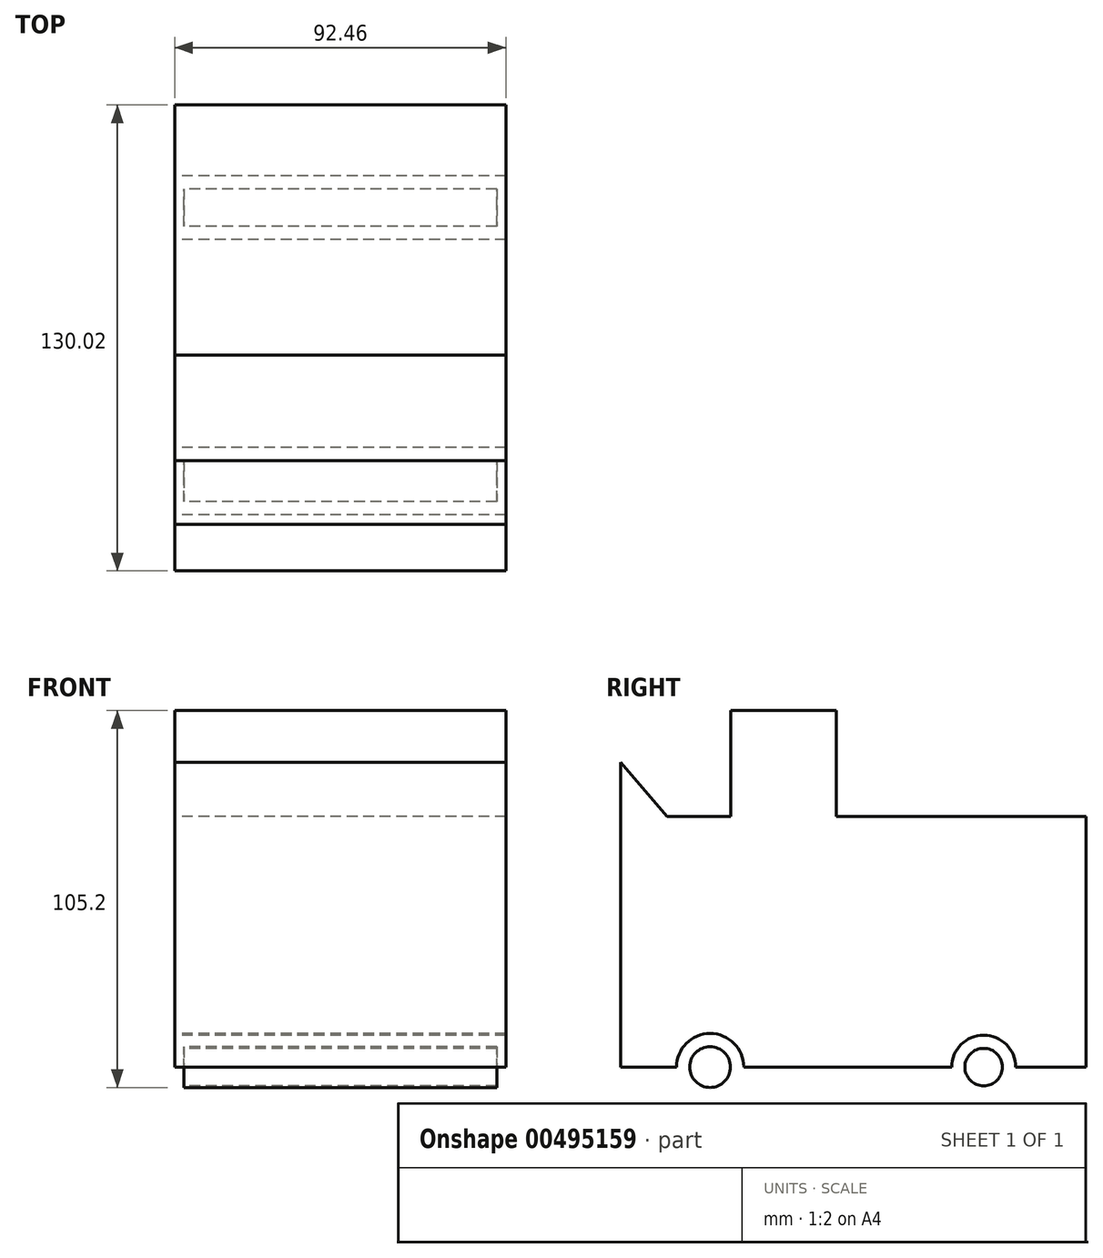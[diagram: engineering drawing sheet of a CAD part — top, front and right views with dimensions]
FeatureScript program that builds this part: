
annotation { "Feature Type Name" : "Feature", "Feature Type Description" : "" }
export const myFeature = defineFeature(function(context is Context, id is Id, definition is map)
    precondition{}
    {
        {
            var Q0;
            Q0=qCreatedBy(makeId("Right.planeOp"),FACE);
            var sketch = newSketch(context, id + "F0", { "sketchPlane" : qUnion([Q0])});
            skLineSegment(sketch, "E0.bottom", {"start": v(-47.3, 5.67) * mm, "end": v(-29.5, 5.67) * mm});
            skLineSegment(sketch, "E0.top", {"start": v(-60.26, -64.34) * mm, "end": v(-44.61, -64.34) * mm});
            skLineSegment(sketch, "E0.left", {"start": v(-60.26, 5.67) * mm, "end": v(-60.26, -64.34) * mm});
            skLineSegment(sketch, "E0.right", {"start": v(69.76, 5.67) * mm, "end": v(69.76, -64.34) * mm});
            skLineSegment(sketch, "E1.top", {"start": v(-29.5, 35.17) * mm, "end": v(0, 35.17) * mm});
            skLineSegment(sketch, "E1.left", {"start": v(-29.5, 5.67) * mm, "end": v(-29.5, 35.17) * mm});
            skLineSegment(sketch, "E1.right", {"start": v(0, 5.67) * mm, "end": v(0, 35.17) * mm});
            skLineSegment(sketch, "E2", {"start": v(-60.26, 5.67) * mm, "end": v(-60.26, 20.77) * mm});
            skLineSegment(sketch, "E3", {"start": v(-60.26, 20.77) * mm, "end": v(-47.3, 5.67) * mm});
            skArc(sketch, "E4", {"start": v(-25.85, -64.34) * mm, "mid": v(-35.23, -54.96) * mm, "end": v(-44.61, -64.34) * mm});
            skArc(sketch, "E5", {"start": v(50.05, -64.34) * mm, "mid": v(41.13, -55.42) * mm, "end": v(32.2, -64.34) * mm});
            skLineSegment(sketch, "E6.trimOffspring", {"start": v(0, 5.67) * mm, "end": v(69.76, 5.67) * mm});
            skLineSegment(sketch, "E7.trimOffspring", {"start": v(-25.85, -64.34) * mm, "end": v(32.2, -64.34) * mm});
            skLineSegment(sketch, "E8.trimOffspring", {"start": v(50.05, -64.34) * mm, "end": v(69.76, -64.34) * mm});
            skSolve(sketch);
        }
        {
            var Q0;
            Q0 = qSketchRegion(id + "F0", true);
            extrude(context, id + "F1", {"entities" : qUnion([Q0]), "endBound" : BoundingType.SYMMETRIC, "depth" : 92.46 * mm});
        }
        {
            var Q0;
            Q0=qCreatedBy(makeId("Right.planeOp"),FACE);
            var sketch = newSketch(context, id + "F2", { "sketchPlane" : qUnion([Q0])});
            skArc(sketch, "E9.0.0", {"start": v(32.2, -64.34) * mm, "mid": v(41.13, -55.42) * mm, "end": v(50.05, -64.34) * mm});
            skArc(sketch, "E9.0.2", {"start": v(50.05, -64.34) * mm, "mid": v(41.13, -55.42) * mm, "end": v(32.2, -64.34) * mm});
            skArc(sketch, "E10.0.0", {"start": v(-44.61, -64.34) * mm, "mid": v(-35.23, -54.96) * mm, "end": v(-25.85, -64.34) * mm});
            skArc(sketch, "E10.0.2", {"start": v(-25.85, -64.34) * mm, "mid": v(-35.23, -54.96) * mm, "end": v(-44.61, -64.34) * mm});
            skCircle(sketch, "E11", {"center": v(-35.23, -64.34) * mm, "radius": 5.69 * mm});
            skCircle(sketch, "E12", {"center": v(41.13, -64.34) * mm, "radius": 5.24 * mm});
            skSolve(sketch);
        }
        {
            var Q0;
            Q0 = qSketchRegion(id + "F2", true);
            extrude(context, id + "F3", {"entities" : qUnion([Q0]), "endBound" : BoundingType.SYMMETRIC, "depth" : 87.38 * mm});
        }
    });
